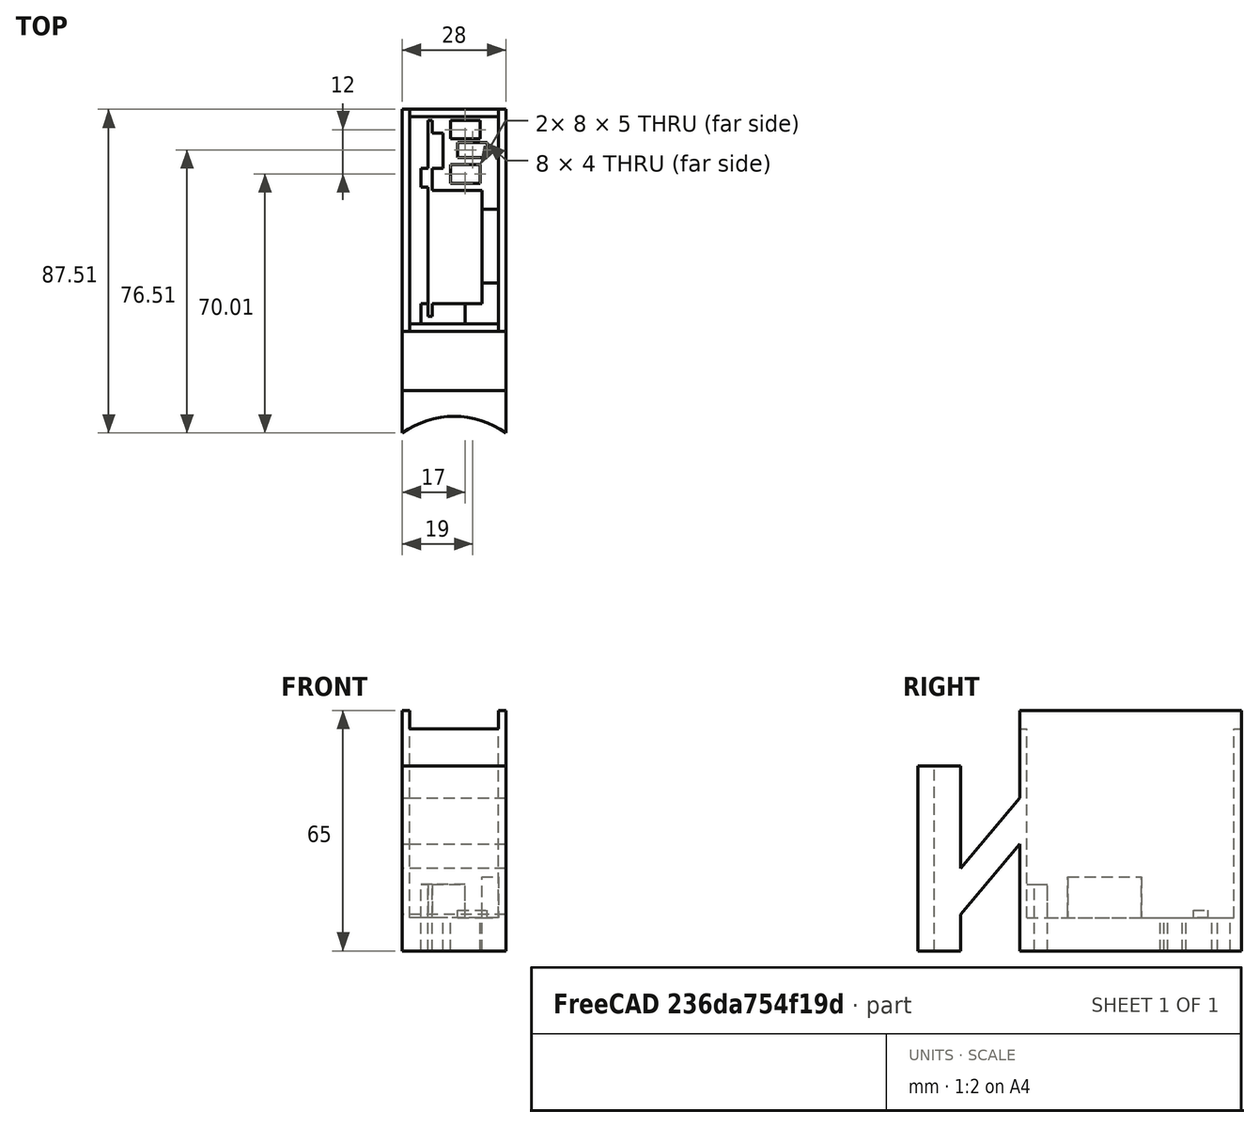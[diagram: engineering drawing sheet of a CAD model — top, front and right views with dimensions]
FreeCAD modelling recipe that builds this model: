
FCSTD DOCUMENT  (FreeCAD 0.15R4671 (Git))
Label: headertest
License: All rights reserved
LicenseURL: http://en.wikipedia.org/wiki/All_rights_reserved
objects: Part::Box×17, Part::MultiFuse×6, Part::Cut×3, Part::Cylinder×1
note: 27 computed .brp shape members not serialized (recipe doc carries the construction recipe); baked Part::Feature solids carry a one-line shape summary decoded from their .brp

FEATURE [Part::Box] Box  label="Cube"
  Height = 20
  Length = 1.1
  Placement = pos=(0,-1,0) rot=(0,0,1;0rad)
  Width = 53
FEATURE [Part::Box] Box001  label="Cube001"
  Height = 10
  Length = 13.5
  Placement = pos=(1,2.5,0) rot=(0,0,1;0rad)
  Width = 30.5
FEATURE [Part::Box] Box002  label="Cube002"
  Height = 10
  Length = 4
  Placement = pos=(0,39,0) rot=(0,0,1;0rad)
  Width = 9.5
FEATURE [Part::Box] Box003  label="Cube003"
  Height = 9
  Length = 26
  Placement = pos=(-5,-5,0) rot=(0,0,1;0rad)
  Width = 60
FEATURE [Part::Box] Box004  label="Cube004"
  Height = 12
  Length = 2
  Placement = pos=(-2,34,0) rot=(0,0,1;0rad)
  Width = 5
FEATURE [Part::MultiFuse] Fusion
  Shapes = -> [Box,Box001,Box002,Box004]
FEATURE [Part::Box] Box005  label="Cube005"
  Height = 11
  Length = 8
  Placement = pos=(8,42,0) rot=(0,0,1;0rad)
  Width = 4
FEATURE [Part::Box] Box006  label="Cube006"
  Height = 20
  Length = 6
  Placement = pos=(14.5,8,0) rot=(0,0,1;0rad)
  Width = 20
FEATURE [Part::Box] Box007  label="Cube007"
  Height = 65
  Length = 2
  Placement = pos=(19,-5,0) rot=(0,0,1;0rad)
  Width = 60
FEATURE [Part::Box] Box008  label="Cube008"
  Height = 65
  Length = 2
  Placement = pos=(-7,-5,0) rot=(0,0,1;0rad)
  Width = 60
FEATURE [Part::Box] Box009  label="Cube009"
  Height = 18
  Length = 12
  Placement = pos=(-2,-5,0) rot=(0,0,1;0rad)
  Width = 7.5
FEATURE [Part::Box] Box010  label="Cube010"
  Height = 60
  Length = 24
  Placement = pos=(-5,-5,0) rot=(0,0,1;0rad)
  Width = 2
FEATURE [Part::Box] Box011  label="Cube011"
  Height = 60
  Length = 24
  Placement = pos=(-5,53,0) rot=(0,0,1;0rad)
  Width = 2
FEATURE [Part::MultiFuse] Fusion001
  Shapes = -> [Box006,Box005,Box003,Box011,Box009,Box008,Box007,Box010]
FEATURE [Part::Cut] Cut
  Base = -> Fusion001
  Tool = -> Fusion
FEATURE [Part::Box] Box012  label="Cube012"
  Height = 40
  Length = 8
  Placement = pos=(6,35,-2) rot=(0,0,1;0rad)
  Width = 5
FEATURE [Part::Box] Box013  label="Cube013"
  Height = 40
  Length = 8
  Placement = pos=(6,47,-2) rot=(0,0,1;0rad)
  Width = 5
FEATURE [Part::MultiFuse] Fusion002
  Shapes = -> [Box012,Box013]
FEATURE [Part::Cut] Cut001
  Base = -> Cut
  Tool = -> Fusion002
FEATURE [Part::Box] Box014  label="Cube014"
  Height = 41
  Length = 28
  Placement = pos=(-7,-28,14) rot=(-1,0,0;0.698132rad)
  Width = 8
FEATURE [Part::Box] Box015  label="Cube015"
  Height = 70
  Length = 36
  Placement = pos=(-11,-4,0) rot=(0,0,1;0rad)
  Width = 37
FEATURE [Part::Box] Box016  label="Cube016"
  Height = 50
  Length = 28
  Placement = pos=(-7,-35,0) rot=(0,0,1;0rad)
  Width = 14
FEATURE [Part::Cylinder] Cylinder
  Angle = 360
  Height = 55
  Placement = pos=(7,-52,-2) rot=(0,0,1;0rad)
  Radius = 24
FEATURE [Part::MultiFuse] Fusion003
  Shapes = -> [Box015,Cylinder]
FEATURE [Part::MultiFuse] Fusion004
  Shapes = -> [Box016,Box014]
FEATURE [Part::Cut] Cut002
  Base = -> Fusion004
  Tool = -> Fusion003
FEATURE [Part::MultiFuse] Fusion005
  Shapes = -> [Cut002,Cut001]
